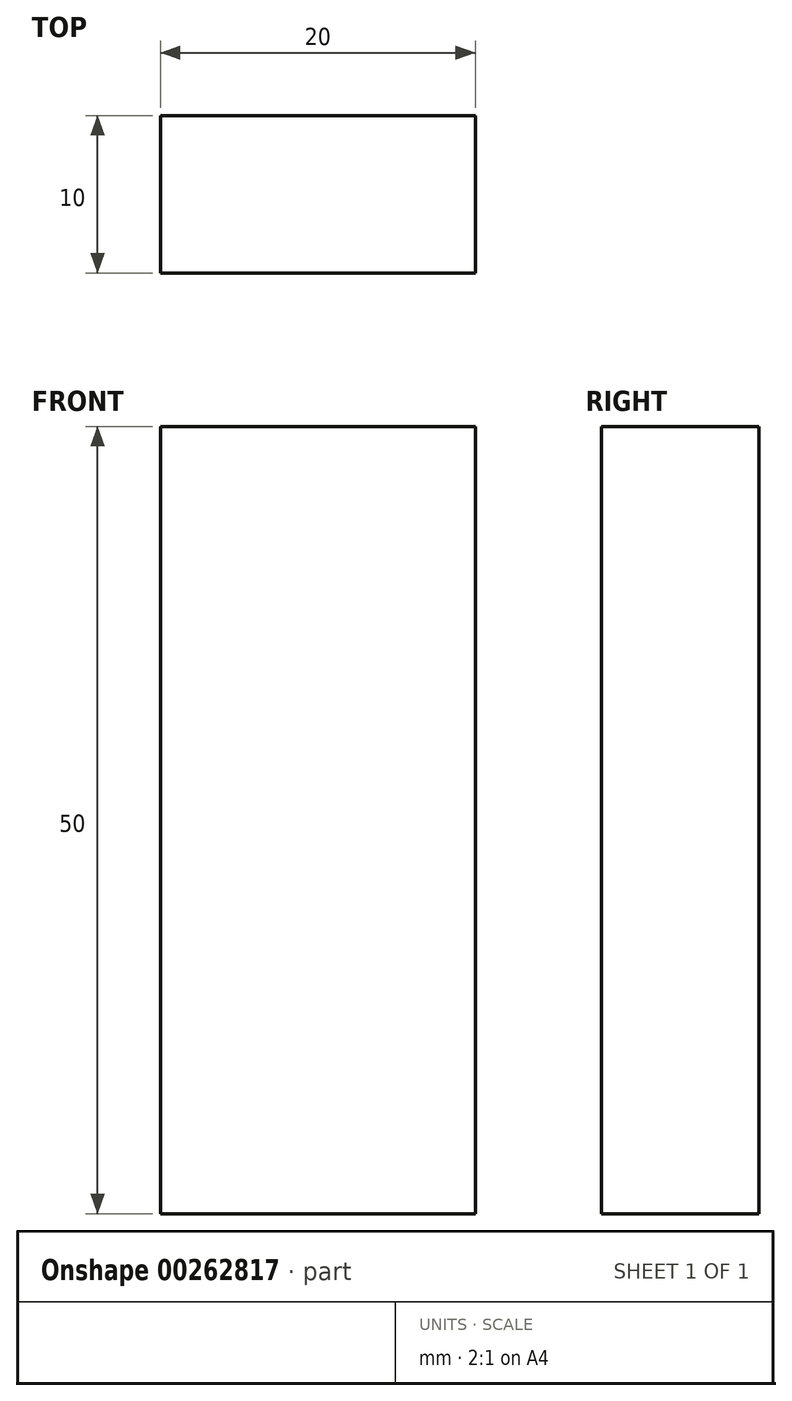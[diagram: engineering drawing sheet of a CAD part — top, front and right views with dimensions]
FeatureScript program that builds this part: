
annotation { "Feature Type Name" : "Feature", "Feature Type Description" : "" }
export const myFeature = defineFeature(function(context is Context, id is Id, definition is map)
    precondition{}
    {
        {
            var Q0;
            Q0=qCreatedBy(makeId("Front.planeOp"),FACE);
            var sketch = newSketch(context, id + "F0", { "sketchPlane" : qUnion([Q0])});
            skLineSegment(sketch, "E0.bottom", {"start": v(-15.23, 37) * mm, "end": v(4.77, 37) * mm});
            skLineSegment(sketch, "E0.top", {"start": v(-15.23, -13) * mm, "end": v(4.77, -13) * mm});
            skLineSegment(sketch, "E0.left", {"start": v(-15.23, 37) * mm, "end": v(-15.23, -13) * mm});
            skLineSegment(sketch, "E0.right", {"start": v(4.77, 37) * mm, "end": v(4.77, -13) * mm});
            skSolve(sketch);
        }
        {
            var Q0;
            Q0=makeQuery(id+"F0.imprint","IMPRINT",FACE,{"disambiguationData":[TD([[makeQuery(id+"F0.imprint","IMPRINT",EDGE,{"derivedFrom":sQuery(id+"F0.wireOp",EDGE,"E0.bottom")}),-1.0]])]});
            extrude(context, id + "F1", {"entities" : qUnion([Q0]), "oppositeDirection" : true, "depth" : 10 * mm});
        }
    });
